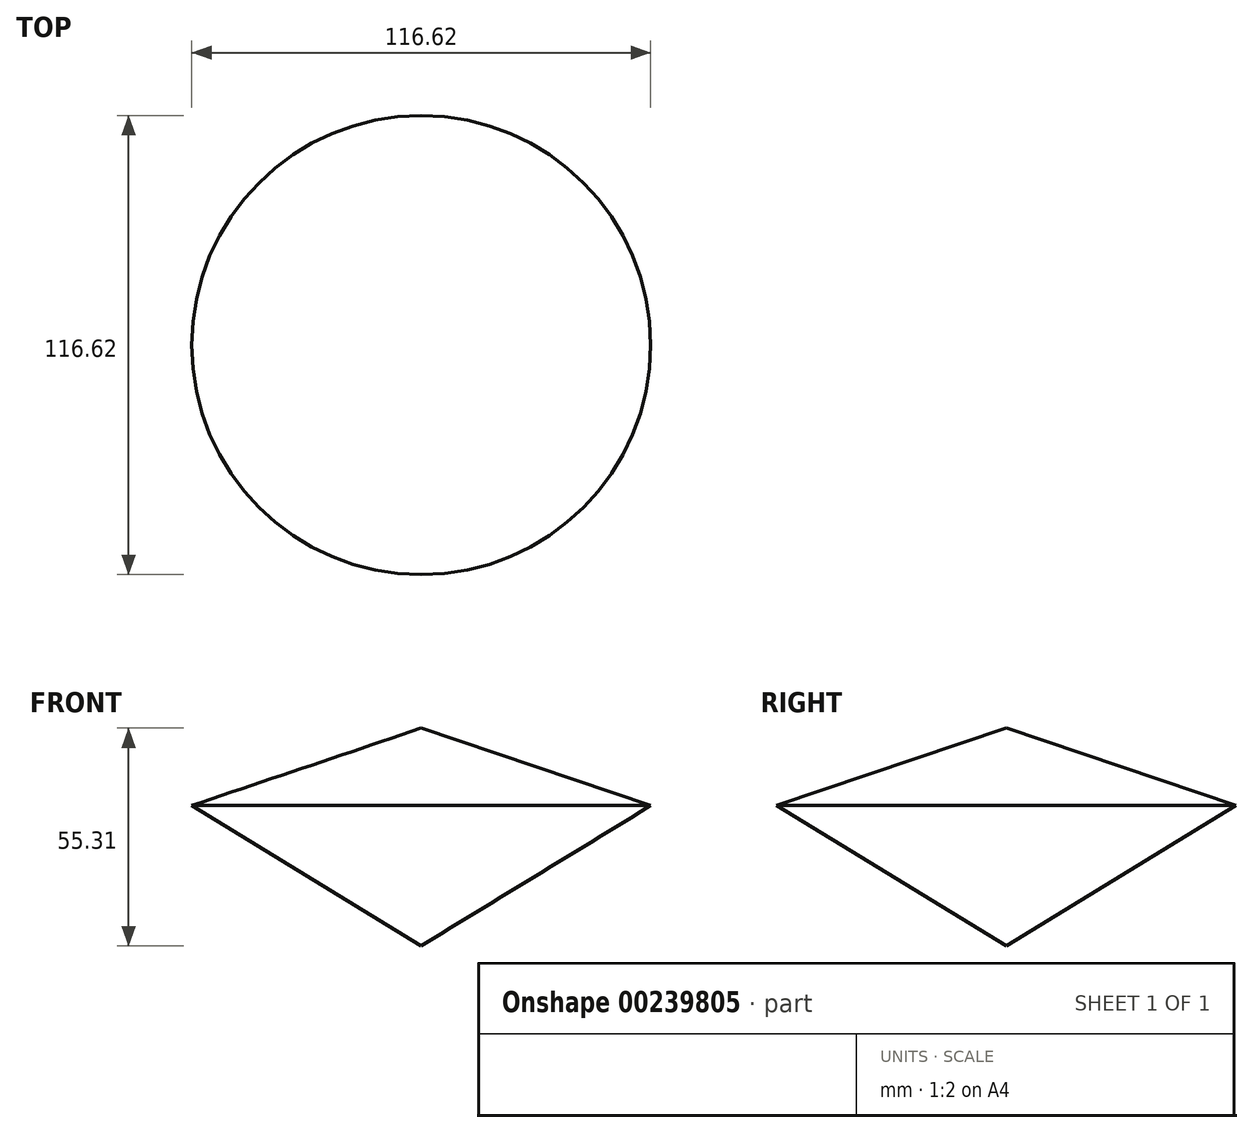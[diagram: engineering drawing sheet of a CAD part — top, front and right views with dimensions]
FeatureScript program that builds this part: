
annotation { "Feature Type Name" : "Feature", "Feature Type Description" : "" }
export const myFeature = defineFeature(function(context is Context, id is Id, definition is map)
    precondition{}
    {
        {
            var Q0;
            Q0=qCreatedBy(makeId("Front.planeOp"),FACE);
            var sketch = newSketch(context, id + "F0", { "sketchPlane" : qUnion([Q0])});
            skLineSegment(sketch, "E0", {"start": v(0, 0) * mm, "end": v(-58.3, 35.65) * mm});
            skLineSegment(sketch, "E1", {"start": v(-58.3, 35.65) * mm, "end": v(0, 55.3) * mm});
            skLineSegment(sketch, "E2", {"start": v(0, 55.3) * mm, "end": v(0, 0) * mm});
            skSolve(sketch);
        }
        {
            var Q0;
            Q0 = qSketchRegion(id + "F0", true);
            var Q1;
            Q1=sQuery(id+"F0.wireOp",EDGE,"E2");
            revolve(context, id + "F1", {"entities" : qUnion([Q0]), "axis" : qUnion([Q1]), "revolveType" : RevolveType.FULL});
        }
    });
